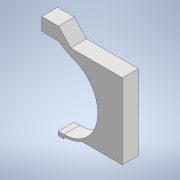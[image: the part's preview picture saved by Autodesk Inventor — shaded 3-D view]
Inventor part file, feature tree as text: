
AUTODESK INVENTOR PART (.ipt)
format: ipt  version: 2022 (Build 260153000, 153)  size: 125,440 bytes
history: native  units: in
note: dims shown in document units (in); Inventor stores cm internally (conversion verified against a paired STEP export)
features: other x4, reference x3, sheet_metal_op x1, sketch x1
ambient origin geometry x8: Origin, YZ Plane, XZ Plane, XY Plane, X Axis, Y Axis, Z Axis, Center Point
bodies: Body1 (feature_tree)
feature tree (9):
  sheet_metal_op  "Face2"
  sketch  "Sketch1"  dims[d1=0.0591in]
  reference  "Reference11"
  reference  "Reference12"
  reference  "Reference13"
  other  "Plate2"
  parser-record x1  (decoder bookkeeping rows leaked as tree rows — omitted from the tree; the rows remain in map.json)
  other  "Assembly1.iam"
  other  "sheetmettaal:1"
note: 1 file-system path scrubbed to <path> (originals preserved in map.json)
